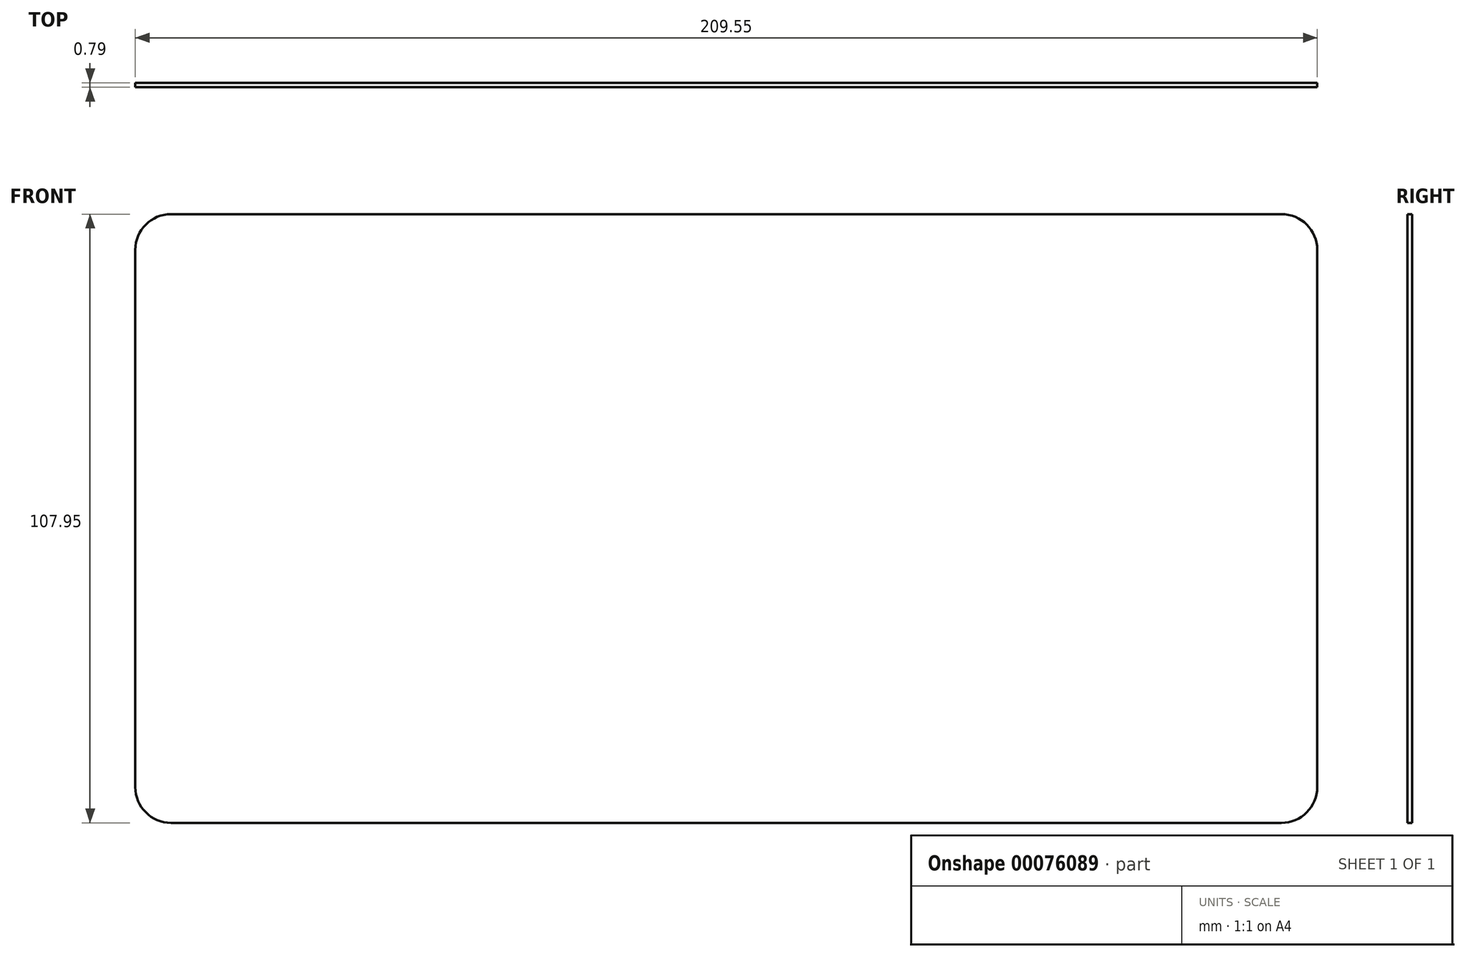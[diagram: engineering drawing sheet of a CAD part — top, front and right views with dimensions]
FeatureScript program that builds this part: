
annotation { "Feature Type Name" : "Feature", "Feature Type Description" : "" }
export const myFeature = defineFeature(function(context is Context, id is Id, definition is map)
    precondition{}
    {
        {
            var Q0;
            Q0=qCreatedBy(makeId("Front.planeOp"),FACE);
            var sketch = newSketch(context, id + "F0", { "sketchPlane" : qUnion([Q0])});
            skLineSegment(sketch, "E0.bottom", {"start": v(-102.11, 49.26) * mm, "end": v(94.74, 49.26) * mm});
            skLineSegment(sketch, "E0.top", {"start": v(-102.11, -58.7) * mm, "end": v(94.74, -58.7) * mm});
            skLineSegment(sketch, "E0.left", {"start": v(-108.46, 42.9) * mm, "end": v(-108.46, -52.34) * mm});
            skLineSegment(sketch, "E0.right", {"start": v(101.09, 42.9) * mm, "end": v(101.09, -52.34) * mm});
            skPoint(sketch, "E1.visualSharp", {"position": v(-108.46, 49.26) * mm});
            skArc(sketch, "E1.filletArc", {"start": v(-102.11, 49.26) * mm, "mid": v(-106.6, 47.4) * mm, "end": v(-108.46, 42.9) * mm});
            skPoint(sketch, "E2.visualSharp", {"position": v(101.09, 49.26) * mm});
            skArc(sketch, "E2.filletArc", {"start": v(101.09, 42.9) * mm, "mid": v(99.23, 47.4) * mm, "end": v(94.74, 49.26) * mm});
            skPoint(sketch, "E3.visualSharp", {"position": v(101.09, -58.7) * mm});
            skArc(sketch, "E3.filletArc", {"start": v(94.74, -58.7) * mm, "mid": v(99.23, -56.83) * mm, "end": v(101.09, -52.34) * mm});
            skPoint(sketch, "E4.visualSharp", {"position": v(-108.46, -58.7) * mm});
            skArc(sketch, "E4.filletArc", {"start": v(-108.46, -52.34) * mm, "mid": v(-106.6, -56.83) * mm, "end": v(-102.11, -58.7) * mm});
            skSolve(sketch);
        }
        {
            var Q0;
            Q0 = qSketchRegion(id + "F0", true);
            extrude(context, id + "F1", {"entities" : qUnion([Q0]), "depth" : 0.8 * mm});
        }
    });
